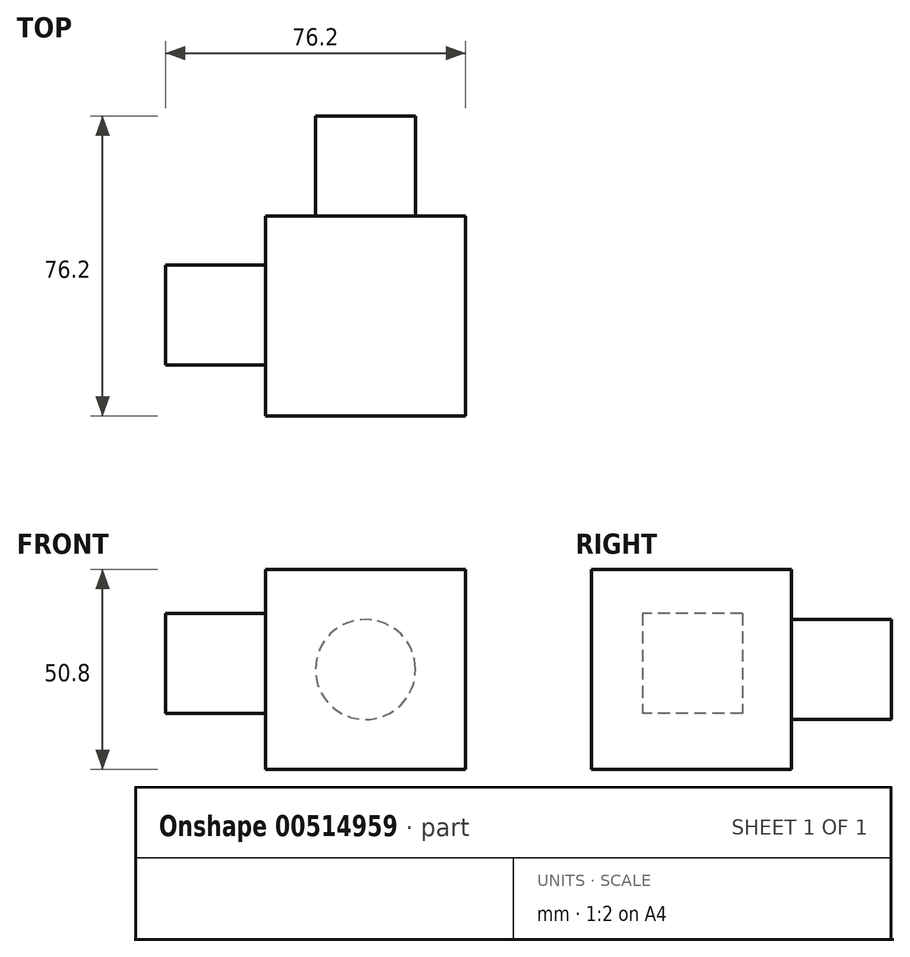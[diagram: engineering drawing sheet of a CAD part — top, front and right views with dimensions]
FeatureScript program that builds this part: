
annotation { "Feature Type Name" : "Feature", "Feature Type Description" : "" }
export const myFeature = defineFeature(function(context is Context, id is Id, definition is map)
    precondition{}
    {
        {
            var Q0;
            Q0=qCreatedBy(makeId("Front.planeOp"),FACE);
            var sketch = newSketch(context, id + "F0", { "sketchPlane" : qUnion([Q0])});
            skLineSegment(sketch, "E0.bottom", {"start": v(-5.85, 50.8) * mm, "end": v(44.95, 50.8) * mm});
            skLineSegment(sketch, "E0.top", {"start": v(-5.85, 0) * mm, "end": v(44.95, 0) * mm});
            skLineSegment(sketch, "E0.left", {"start": v(-5.85, 50.8) * mm, "end": v(-5.85, 0) * mm});
            skLineSegment(sketch, "E0.right", {"start": v(44.95, 50.8) * mm, "end": v(44.95, 0) * mm});
            skSolve(sketch);
        }
        {
            var Q0;
            Q0 = qSketchRegion(id + "F0", true);
            extrude(context, id + "F1", {"entities" : qUnion([Q0]), "depth" : 50.8 * mm, "offsetDistance" : 25.4 * mm});
        }
        {
            var Q0;
            Q0=qCreatedBy(makeId("Front.planeOp"),FACE);
            var sketch = newSketch(context, id + "F2", { "sketchPlane" : qUnion([Q0])});
            skCircle(sketch, "E1", {"center": v(19.55, 25.4) * mm, "radius": 12.7 * mm});
            skSolve(sketch);
        }
        {
            var Q0;
            Q0=makeQuery(id+"F2.imprint","IMPRINT",FACE,{"disambiguationData":[TD([[makeQuery(id+"F2.imprint","IMPRINT",EDGE,{"derivedFrom":sQuery(id+"F2.wireOp",EDGE,"E1")}),1.0]])]});
            extrude(context, id + "F3", {"entities" : qUnion([Q0]), "operationType" : NewBodyOperationType.ADD, "oppositeDirection" : true, "depth" : 25.4 * mm, "offsetDistance" : 25.4 * mm});
        }
        {
            var Q0;
            Q0=makeQuery(id+"F1.opExtrude","SWEPT_FACE",FACE,{"disambiguationData":[OSD([sQuery(id+"F0.wireOp",EDGE,"E0.left")])]});
            var sketch = newSketch(context, id + "F4", { "sketchPlane" : qUnion([Q0])});
            skLineSegment(sketch, "E2.bottom", {"start": v(12.48, 39.63) * mm, "end": v(37.88, 39.63) * mm});
            skLineSegment(sketch, "E2.top", {"start": v(12.48, 14.23) * mm, "end": v(37.88, 14.23) * mm});
            skLineSegment(sketch, "E2.left", {"start": v(12.48, 39.63) * mm, "end": v(12.48, 14.23) * mm});
            skLineSegment(sketch, "E2.right", {"start": v(37.88, 39.63) * mm, "end": v(37.88, 14.23) * mm});
            skSolve(sketch);
        }
        {
            var Q0;
            Q0 = qSketchRegion(id + "F4", true);
            extrude(context, id + "F5", {"entities" : qUnion([Q0]), "operationType" : NewBodyOperationType.ADD, "depth" : 25.4 * mm, "offsetDistance" : 25.4 * mm});
        }
    });
